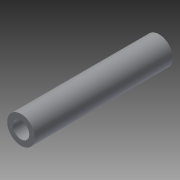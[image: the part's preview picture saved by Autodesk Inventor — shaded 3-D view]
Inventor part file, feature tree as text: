
AUTODESK INVENTOR PART (.ipt)
format: ipt  version: 2015 (Build 190159000, 159)  size: 75,264 bytes
history: native  units: mm
features: extrude x1, sketch x1
ambient origin geometry x8: Origin, YZ Plane, XZ Plane, XY Plane, X Axis, Y Axis, Z Axis, Center Point
bodies: Solid1 (feature_tree)
feature tree (2):
  extrude  "Extrusion1"  Depth=25.0mm
  sketch  "Sketch1"  dims[d0=3.0mm d1=5.0mm d2=25.0mm d3=0.0mm]
